# Revit family: LC1501
name_source: partatom
category: Luminarias
units: mm (PartAtom-declared; Revit-internal decimal feet)

## family parameters
Compartido = Sí
Corte con vacíos al cargar = No
Cota de conector redondo = Diámetro de uso
Origen de luz = No
Punto de cálculo de habitación = No
Se basa en plano de trabajo = Sí
Siempre vertical = No
Tipo de pieza = Normal

## types (1)
- PERFIL_LC1501
    Clips de Sujecion 1501.2 = 3
    Descripción = PERFIL DE ALUMINIO CON DIFUSOR LECHOSO DE 8MM EFECTO NEON, PARA ALOJAR TIRA LUMINOSA DE HASTA 17MM DE ANCHO. INSTALACION EMPOTRADO PARA PISO CON PERFIL DE PROTECCION. IDEAL PARA ATENUAR EL BRILLO E INCORPORAR LA LUZ AL AMBIENTE.PRESENTACION DE 1 METRO. IK10, REQUEIRE ACCESORIOS COMO TAPA FINAL PARA EXTREMOS Y CLIPS DE SUJECION (CONSIDERAR 4 PZAS POR 1.0M), SOLERA Y PERFIL DE ALUMINIO.
    Elevación por defecto = 1219 mm
    Fabricante = BRILLANT
    Longitud = 1000 mm  [stored 3.28084 ft]
    Modelo = LC1501
    Perfil de Aluminio LTB-1501 = 1
    Solera 1501.3 = 1
    Tapa Final 1501.1 = 1

note: [stored X ft] marks values corroborated as IEEE doubles in the binary element streams (Revit-internal decimal feet)

## geometry (parser evidence)
native form markers: Blend x2
no freeform markers — native parametric forms only
